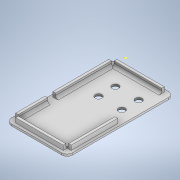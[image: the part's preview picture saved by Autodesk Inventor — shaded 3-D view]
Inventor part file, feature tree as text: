
AUTODESK INVENTOR PART (.ipt)
format: ipt  version: 2022 (Build 260153000, 153)  size: 911,872 bytes
history: native  units: mm
features: extrude x19, sketch x19, fillet x7, other x3, plane x2, chamfer x1, move_body x1, shell x1
ambient origin geometry x8: Origin, YZ Plane, XZ Plane, XY Plane, X Axis, Y Axis, Z Axis, Center Point
bodies: Body1 (feature_tree), Body2 (feature_tree), Body3 (feature_tree), Body4 (feature_tree)
feature tree (53):
  other  "Control"
  extrude  "Extrusion1"  Depth=28.8mm
  extrude  "Extrusion2"  Depth=14.7mm
  extrude  "Extrusion3"  Depth=2.36mm
  extrude  "Extrusion4"  Depth=7.9mm
  extrude  "Extrusion6"  Depth=8.55mm
  extrude  "Extrusion7"  Depth=2.36mm
  chamfer  "Chamfer1"  Distance=8.5mm
  extrude  "Extrusion8"  Depth=10.17mm
  extrude  "Extrusion9"  Depth=11.0mm
  plane  "Work Plane2"
  extrude  "Extrusion10"  Depth=9.44mm
  extrude  "Extrusion11"  Depth=4.82mm
  extrude  "Extrusion12"  Depth=10.0mm
  move_body  "Move Body1"
  plane  "Work Plane4"
  extrude  "Extrusion13"  Depth=0.4mm
  extrude  "Extrusion14"  Depth=11.13mm
  extrude  "Extrusion15"  Depth=0.61mm
  sketch  "Sketch16"  dims[d40=12.7mm d41=11.13mm]
  extrude  "Extrusion16"  Depth=0.61mm
  extrude  "Extrusion17"  Depth=0.61mm
  fillet  "Fillet1"  Radius=0.61mm
  fillet  "Fillet2"  Radius=1.0mm
  fillet  "Fillet3"  Radius=1.0mm
  extrude  "Extrusion18"  Depth=2.085mm
  extrude  "Extrusion19"  Depth=2.0mm
  extrude  "Extrusion20"  Depth=2.0mm
  fillet  "Fillet4"  Radius=5.8mm
  fillet  "Fillet5"  Radius=2.0mm
  fillet  "Fillet6"  Radius=0.4mm
  fillet  "Fillet7"  Radius=0.2mm
  sketch  "Sketch1"  dims[d0=29.4mm d1=28.8mm]
  sketch  "Sketch2"  dims[d2=14.4mm d3=14.7mm]
  sketch  "Sketch3"  dims[d4=1.57mm d5=0.0mm d6=2.36mm]
  sketch  "Sketch4"  dims[d7=11.49mm d8=7.9mm]
  sketch  "Sketch6"  dims[d9=0.77mm d10=8.55mm]
  sketch  "Sketch7"  dims[d11=0.6mm d12=2.36mm]
  sketch  "Sketch8"  dims[d13=0.4mm d14=8.5mm d15=0.0mm]
  other  "Buttons"
  sketch  "Sketch9"  dims[d16=10.15mm d17=10.17mm]
  sketch  "Sketch11"  dims[d18=5.0mm d19=11.0mm]
  sketch  "Sketch12"  dims[d20=8.0mm d21=0.0mm d22=9.44mm]
  sketch  "Sketch13"  dims[d23=4.82mm d24=4.82mm]
  sketch  "Sketch14"  dims[d25=7.0mm d26=10.0mm d27=0.0mm d28=0.0mm d37=4.97mm]
  sketch  "Sketch15"  dims[d38=8.0mm d39=0.4mm]
  sketch  "Sketch17"  dims[d42=2.55mm d43=0.0mm d44=0.61mm]
  sketch  "Sketch18"  dims[d45=0.61mm d46=0.61mm]
  sketch  "Sketch19"  dims[d47=0.61mm d48=0.61mm d49=0.61mm d50=1.0mm d51=1.0mm]
  other  "Lid"
  shell  "Shell"  Thickness=0.2mm
  sketch  "Sketch20"  dims[d52=2.085mm d53=2.085mm]
  sketch  "Sketch21"  dims[d54=1.9mm d55=0.925mm d56=0.925mm d57=5.8mm d58=0.0mm d59=0.2mm d60=2.0mm d61=45.0deg d62=0.4mm d63=0.2mm d64=0.2mm d65=1.9425mm d66=0.4mm d67=0.4mm d68=0.4mm d69=1.9425mm d70=2.0mm d71=2.0mm d72=2.005mm d73=0.2mm d74=0.2mm d75=0.2mm d76=0.2mm d77=0.2mm d83=2.2mm d84=0.2mm d85=2.2mm d86=2.345mm d90=0.4mm d91=0.4mm d92=0.2mm d93=2.54mm d94=0.0mm d102=0.61mm d103=0.61mm d112=0.2mm d113=0.2mm d114=0.4mm d115=0.2mm d117=2.345mm d118=1.075mm d119=0.875mm d120=0.875mm d121=2.3mm d122=0.61mm d123=0.61mm d124=0.61mm d125=2.3mm d126=2.3mm d127=1.075mm d128=2.65mm d129=0.0mm d130=28.7mm d131=32.7mm d134=1.6mm d135=0.0mm d136=6.0mm d137=6.0mm d138=6.0mm d139=6.0mm d140=2.3mm d141=11.53mm d142=2.6mm d143=6.7mm d144=4.0mm d145=0.0mm d146=3.5mm d147=3.5mm d148=3.5mm d149=3.5mm d150=3.0mm d151=3.0mm d152=3.0mm d153=3.0mm d154=4.55mm d155=-0.349066mm d158=180.0deg d159=5.0mm d160=-14.0mm d161=-8.0mm d162=2.0mm d163=45.0mm d164=3.0mm d165=13.0mm d166=2.5mm d167=7.0mm d168=10.0mm d173=1.5mm d174=0.0mm d175=2.0mm d176=2.0mm d177=2.0mm d178=2.0mm d179=30.0mm d180=0.0mm d181=1.0mm d182=2.0mm d183=22.0mm d184=0.0mm d185=45.813165mm d187=24.5mm d188=2.313165mm d189=4.0mm d190=1.0mm d191=2.0mm d192=2.0mm d193=2.0mm d194=1.0mm d195=2.0mm d197=15.0mm d199=25.0mm d200=11.3mm d201=23.0mm d202=22.813165mm d203=22.0mm d204=-2.094395mm d205=4.0mm d206=5.0mm d207=4.0mm d208=22.0mm d209=0.0mm d210=4.0mm d211=3.0mm d212=1.0mm d213=4.0mm d214=5.0mm d215=5.0mm d216=5.0mm d217=5.0mm d218=1.5mm d219=0.0mm d220=25.0mm d221=11.3mm d222=32.2mm d224=2.0mm d225=2.0mm d226=2.0mm d228=2.0mm d231=1.015mm d232=1.015mm d233=1.0mm d234=1.0mm d235=3.0mm d236=3.0mm d237=35.0mm d238=2.0mm d239=22.0mm d240=6.0mm d241=2.0mm d242=3.5mm d243=0.0mm d244=10.0mm d245=8.0mm d246=3.0mm d247=2.0mm d248=4.0mm d249=0.0mm d250=8.0mm d251=2.0mm d252=5.0mm d253=11.0mm d254=3.0mm d255=2.0mm d256=10.25mm d257=0.0mm d258=1.0mm d259=1.0mm d260=1.0mm d261=2.0mm]
